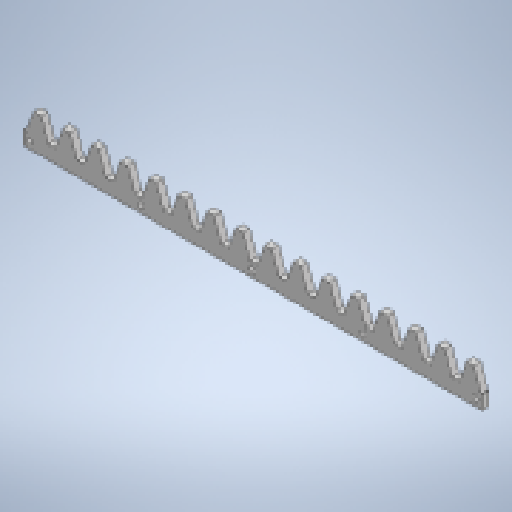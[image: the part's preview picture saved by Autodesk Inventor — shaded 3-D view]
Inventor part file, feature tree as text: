
AUTODESK INVENTOR PART (.ipt)
format: ipt  version: 2024 (Build 280153000, 153)  size: 452,096 bytes
history: native  units: mm
features: extrude x5, sketch x5, projected_geometry x2, pattern_linear x1
ambient origin geometry x8: Origin, YZ Plane, XZ Plane, XY Plane, X Axis, Y Axis, Z Axis, Center Point
bodies: Solid1 (feature_tree)
feature tree (13):
  extrude  "Extrusion1"  Depth=40.0mm TaperAngle=0.0deg
  extrude  "Extrusion2"  Depth=200.0mm
  pattern_linear  "Rectangular Pattern1"  Spacing1=0.0mm  [1 undecoded]
  extrude  "押し出し3"  Depth=18.0mm TaperAngle=0.0deg
  extrude  "押し出し4"  Depth=18.0mm
  extrude  "押し出し5"  Depth=18.0mm
  sketch  "Sketch_4"  dims[d0=40.0mm d1=0.0mm d2=40.0mm d3=0.0mm]
  sketch  "Sketch_5"  dims[d4=420.0mm d6=12.56636mm d7=10.0mm d9=0.0mm d10=200.0mm d11=0.0mm d12=0.0mm d13=37.0mm d14=0.0mm d15=18.0mm d16=2.6mm d17=2.6mm d18=2.6mm d19=0.0mm d20=0.0mm]
  sketch  "スケッチ3"
  projected_geometry  "投影ループ1"
  sketch  "スケッチ4"
  projected_geometry  "投影ループ2"
  sketch  "スケッチ5"
note: 1 required parameter value undecoded (feature->parameter linkage not recoverable at this tier; creation-order binding heuristic only, values carry confidence <= 0.55)
